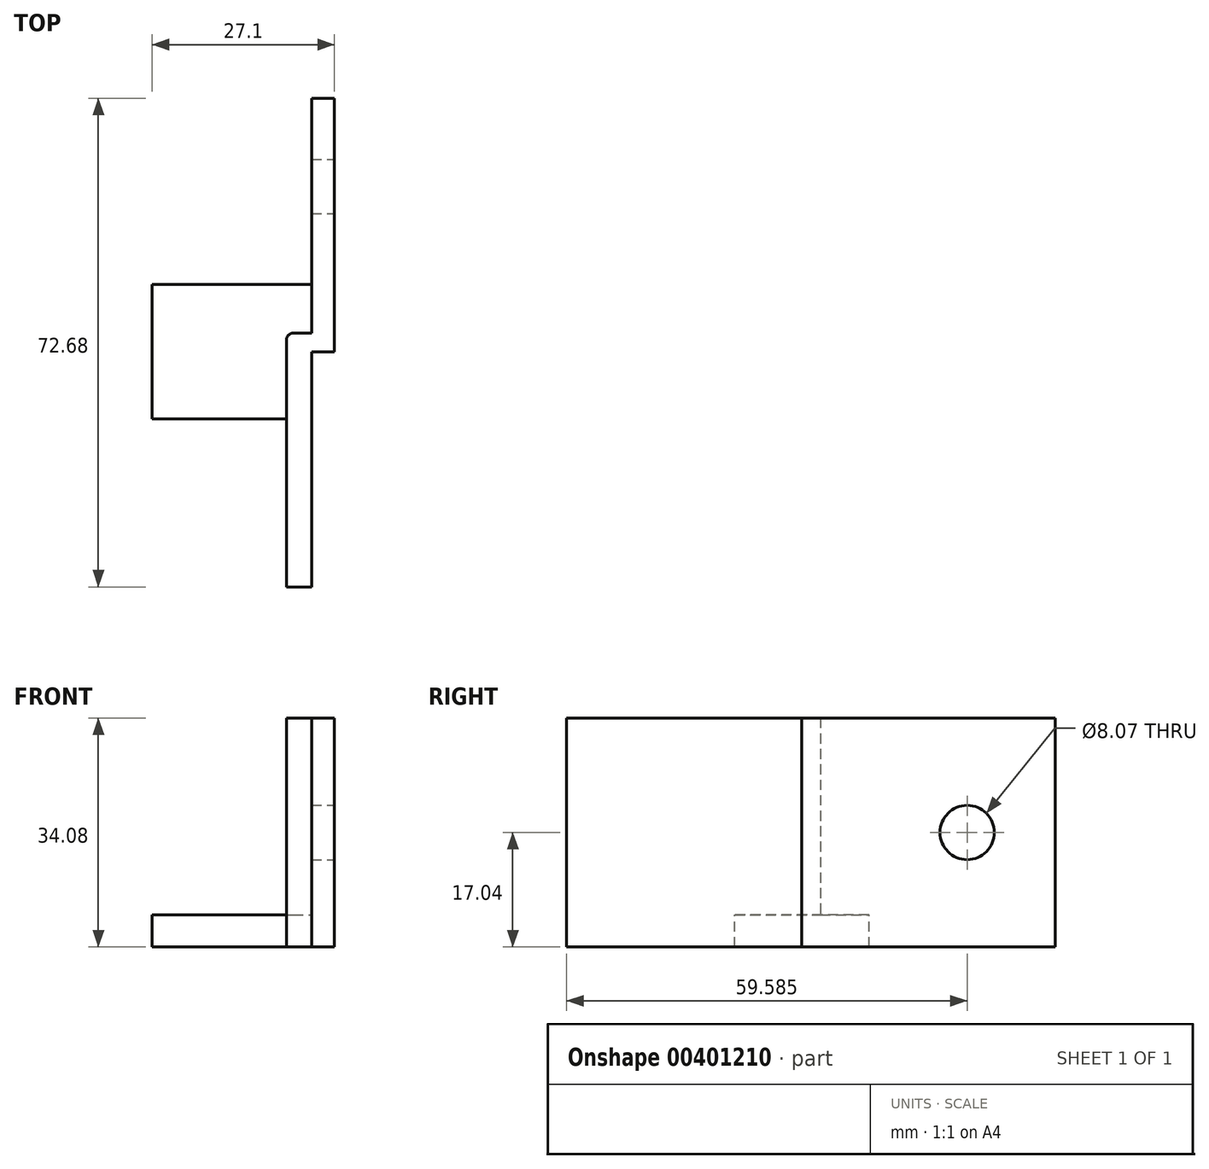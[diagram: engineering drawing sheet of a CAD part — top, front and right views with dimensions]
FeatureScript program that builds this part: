
annotation { "Feature Type Name" : "Feature", "Feature Type Description" : "" }
export const myFeature = defineFeature(function(context is Context, id is Id, definition is map)
    precondition{}
    {
        {
            var Q0;
            Q0=qCreatedBy(makeId("Top.planeOp"),FACE);
            var sketch = newSketch(context, id + "F0", { "sketchPlane" : qUnion([Q0]), "asVersion" : FeatureScriptVersionNumber.V626_COLLAPSE_ARRAY_ITEMS_UIHINT});
            skLineSegment(sketch, "E0", {"start": v(23.7, 37.69) * mm, "end": v(23.7, 2.76) * mm});
            skLineSegment(sketch, "E1", {"start": v(23.7, 2.76) * mm, "end": v(19.97, 2.76) * mm});
            skLineSegment(sketch, "E2", {"start": v(19.97, 2.76) * mm, "end": v(19.97, -35) * mm});
            skLineSegment(sketch, "E3", {"start": v(19.97, -35) * mm, "end": v(23.7, -35) * mm});
            skLineSegment(sketch, "E4", {"start": v(23.7, -35) * mm, "end": v(23.7, 0) * mm});
            skLineSegment(sketch, "E5", {"start": v(23.7, 0) * mm, "end": v(27.1, 0) * mm});
            skLineSegment(sketch, "E6", {"start": v(27.1, 0) * mm, "end": v(27.1, 37.69) * mm});
            skLineSegment(sketch, "E7", {"start": v(27.1, 37.7) * mm, "end": v(23.7, 37.7) * mm});
            skSolve(sketch);
        }
        {
            var Q0;
            Q0 = qSketchRegion(id + "F0", true);
            extrude(context, id + "F1", {"entities" : qUnion([Q0]), "depth" : 34.08 * mm});
        }
        {
            var Q0;
            Q0=makeQuery(id+"F1.opExtrude","SWEPT_FACE",FACE,{"disambiguationData":[OSD([sQuery(id+"F0.wireOp",EDGE,"E6")])]});
            var sketch = newSketch(context, id + "F2", { "sketchPlane" : qUnion([Q0]), "asVersion" : FeatureScriptVersionNumber.V626_COLLAPSE_ARRAY_ITEMS_UIHINT});
            skArc(sketch, "E8", {"start": v(24.6, 34.08) * mm, "mid": v(41.63, 17.04) * mm, "end": v(24.6, 0) * mm});
            skPoint(sketch, "E8.centerSnap0", {"position": v(37.69, 17.04) * mm});
            skCircle(sketch, "E9", {"center": v(24.6, 17.04) * mm, "radius": 4.04 * mm});
            skLineSegment(sketch, "E10.bottom", {"start": v(-9.98, 0) * mm, "end": v(9.98, 0) * mm});
            skLineSegment(sketch, "E10.top", {"start": v(-9.99, 4.77) * mm, "end": v(9.99, 4.77) * mm});
            skLineSegment(sketch, "E10.left", {"start": v(-9.98, 0) * mm, "end": v(-9.98, 4.77) * mm});
            skLineSegment(sketch, "E10.right", {"start": v(9.98, 0) * mm, "end": v(9.98, 4.77) * mm});
            skPoint(sketch, "E11", {"position": v(-18.2, 34.1) * mm});
            skSolve(sketch);
        }
        {
            var Q0;
            Q0=makeQuery(id+"F2.imprint","IMPRINT",FACE,{"disambiguationData":[TD([[makeQuery(id+"F2.imprint","IMPRINT",EDGE,{"derivedFrom":sQuery(id+"F2.wireOp",EDGE,"E9")}),1.0]])]});
            var Q1;
            {var subQ0=sQuery(id+"F2.wireOp",EDGE,"E8");var subQ1=sQuery(id+"F0.wireOp",EDGE,"E6");var subQ2=makeQuery(id+"F1.opExtrude","CAP_EDGE",EDGE,{"disambiguationData":[OSD([subQ1])],"isStart":false});var subQ3=makeQuery(id+"F2.imprint","INTERSECT",VERTEX,{"derivedFrom":[subQ2,subQ0]});Q1=makeQuery(id+"F2.imprint","IMPRINT",FACE,{"disambiguationData":[TD([[makeQuery(id+"F2.imprint","IMPRINT",EDGE,{"disambiguationData":[TD([[subQ3,-1.0]])],"derivedFrom":subQ0}),1.0]])]});}
            var Q2;
            {var subQ0=sQuery(id+"F2.wireOp",EDGE,"E8");var subQ1=sQuery(id+"F0.wireOp",EDGE,"E6");var subQ2=makeQuery(id+"F1.opExtrude","CAP_EDGE",EDGE,{"disambiguationData":[OSD([subQ1])],"isStart":true});var subQ3=makeQuery(id+"F2.imprint","INTERSECT",VERTEX,{"derivedFrom":[subQ2,subQ0]});Q2=makeQuery(id+"F2.imprint","IMPRINT",FACE,{"disambiguationData":[TD([[makeQuery(id+"F2.imprint","IMPRINT",EDGE,{"disambiguationData":[TD([[subQ3,1.0]])],"derivedFrom":subQ0}),1.0]])]});}
            extrude(context, id + "F3", {"entities" : qUnion([Q0, Q1, Q2]), "operationType" : NewBodyOperationType.REMOVE, "endBound" : BoundingType.THROUGH_ALL, "oppositeDirection" : true, "depth" : 25 * mm});
        }
        {
            var Q0;
            {var subQ0=sQuery(id+"F2.wireOp",EDGE,"E8");var subQ1=sQuery(id+"F0.wireOp",EDGE,"E7");var subQ2=sQuery(id+"F0.wireOp",EDGE,"E6");Q0=makeQuery(id+"F3.boolean.opBoolean","COPY",EDGE,{"derivedFrom":makeQuery(id+"F3.opExtrude","SWEPT_EDGE",EDGE,{"disambiguationData":[OSD([subQ2,subQ1,subQ0]),TDD([makeQuery(id+"F2.imprint","INTERSECT",VERTEX,{"disambiguationData":[OD(0.0)],"derivedFrom":[makeQuery(id+"F1.opExtrude","SWEPT_EDGE",EDGE,{"disambiguationData":[OSD([subQ2,subQ1])]}),subQ0]})])]})});}
            var Q1;
            {var subQ0=sQuery(id+"F2.wireOp",EDGE,"E8");var subQ1=sQuery(id+"F0.wireOp",EDGE,"E7");var subQ2=sQuery(id+"F0.wireOp",EDGE,"E6");Q1=makeQuery(id+"F3.boolean.opBoolean","COPY",EDGE,{"derivedFrom":makeQuery(id+"F3.opExtrude","SWEPT_EDGE",EDGE,{"disambiguationData":[OSD([subQ2,subQ1,subQ0]),TDD([makeQuery(id+"F2.imprint","INTERSECT",VERTEX,{"disambiguationData":[OD(1.0)],"derivedFrom":[makeQuery(id+"F1.opExtrude","SWEPT_EDGE",EDGE,{"disambiguationData":[OSD([subQ2,subQ1])]}),subQ0]})])]})});}
            var Q2;
            Q2=makeQuery(id+"F1.opExtrude","SWEPT_EDGE",EDGE,{"disambiguationData":[OSD([sQuery(id+"F0.wireOp",EDGE,"E1"),sQuery(id+"F0.wireOp",EDGE,"E2")])]});
            fillet(context, id + "F4", {"entities" : qUnion([Q0, Q1, Q2]), "radius" : 1 * mm, "tangentPropagation" : true, "allowEdgeOverflow" : false});
        }
        {
            var Q0;
            {var subQ4=sQuery(id+"F2.wireOp",EDGE,"E10.right");Q0=makeQuery(id+"F2.imprint","IMPRINT",FACE,{"disambiguationData":[TD([[makeQuery(id+"F2.imprint","IMPRINT",EDGE,{"derivedFrom":subQ4}),1.0]])]});}
            var Q1;
            Q1=qCreatedBy(makeId("Right.planeOp"),FACE);
            extrude(context, id + "F5", {"entities" : qUnion([Q0]), "operationType" : NewBodyOperationType.ADD, "endBound" : BoundingType.UP_TO_SURFACE, "oppositeDirection" : true, "endBoundEntityFace" : qUnion([Q1]), "depth" : 25 * mm});
        }
        {
            var Q0;
            {var subQ3=sQuery(id+"F2.wireOp",EDGE,"E10.left");Q0=makeQuery(id+"F2.imprint","IMPRINT",FACE,{"disambiguationData":[TD([[makeQuery(id+"F2.imprint","IMPRINT",EDGE,{"derivedFrom":subQ3}),-1.0]])]});}
            var Q1;
            Q1=qCreatedBy(makeId("Right.planeOp"),FACE);
            var Q2;
            Q2=makeQuery(id+"F1.opExtrude","SWEPT_FACE",FACE,{"disambiguationData":[OSD([sQuery(id+"F0.wireOp",EDGE,"E4")])]});
            var Q3;
            Q3=makeQuery(id+"F1.opExtrude","SWEPT_BODY",BODY,{"disambiguationData":[OSD([sQuery(id+"F0.wireOp",EDGE,"E0"),sQuery(id+"F0.wireOp",EDGE,"E1"),sQuery(id+"F0.wireOp",EDGE,"E2"),sQuery(id+"F0.wireOp",EDGE,"E3"),sQuery(id+"F0.wireOp",EDGE,"E4"),sQuery(id+"F0.wireOp",EDGE,"E5"),sQuery(id+"F0.wireOp",EDGE,"E6"),sQuery(id+"F0.wireOp",EDGE,"E7")])]});
            extrude(context, id + "F6", {"entities" : qUnion([Q0]), "operationType" : NewBodyOperationType.ADD, "endBound" : BoundingType.UP_TO_SURFACE, "oppositeDirection" : true, "endBoundEntityFace" : qUnion([Q1]), "depth" : 25 * mm, "hasSecondDirection" : true, "secondDirectionBound" : BoundingType.UP_TO_SURFACE, "secondDirectionOppositeDirection" : true, "secondDirectionBoundEntityFace" : qUnion([Q2]), "secondDirectionBoundEntityBody" : qUnion([Q3]), "secondDirectionDepth" : 25 * mm});
        }
    });
